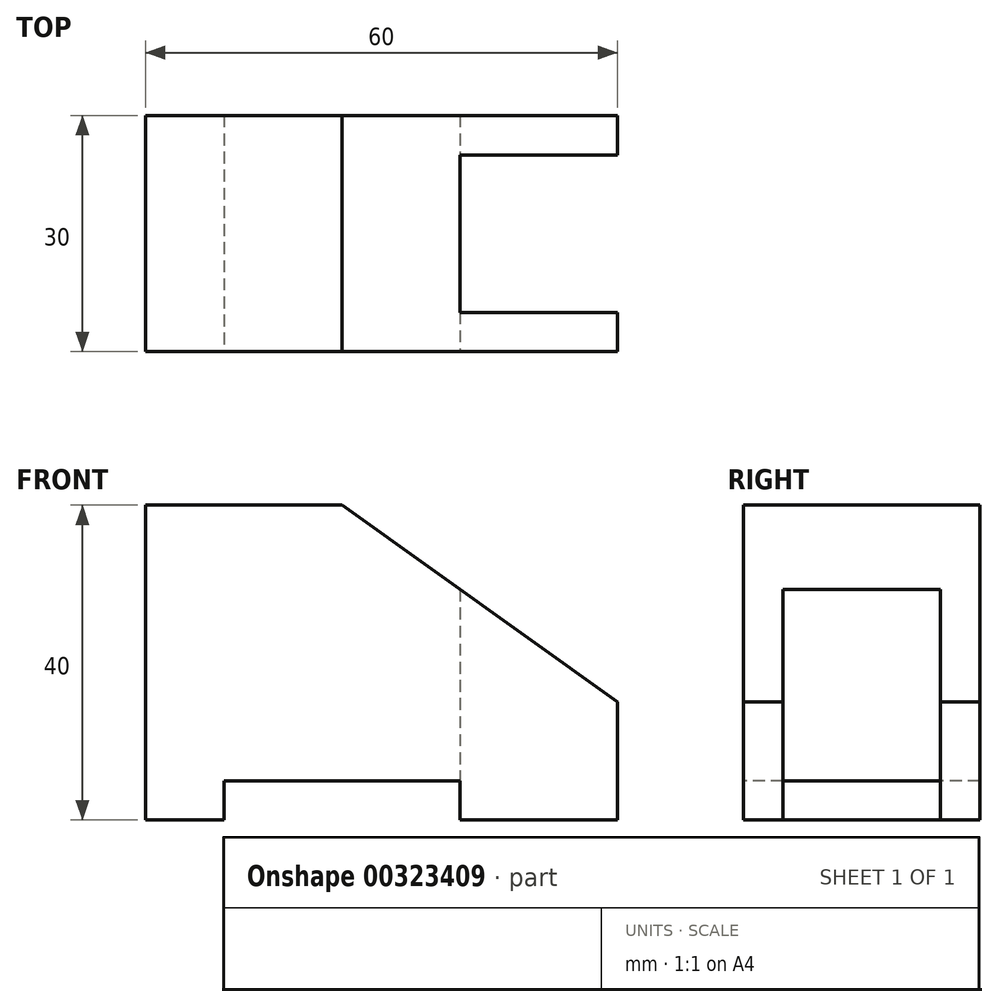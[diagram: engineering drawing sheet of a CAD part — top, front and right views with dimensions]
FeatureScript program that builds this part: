
annotation { "Feature Type Name" : "Feature", "Feature Type Description" : "" }
export const myFeature = defineFeature(function(context is Context, id is Id, definition is map)
    precondition{}
    {
        {
            var Q0;
            Q0=qCreatedBy(makeId("Front.planeOp"),FACE);
            var sketch = newSketch(context, id + "F0", { "sketchPlane" : qUnion([Q0])});
            skLineSegment(sketch, "E0.bottom", {"start": v(0, 0) * mm, "end": v(60, 0) * mm});
            skLineSegment(sketch, "E0.top", {"start": v(0, 40) * mm, "end": v(60, 40) * mm});
            skLineSegment(sketch, "E0.left", {"start": v(0, 0) * mm, "end": v(0, 40) * mm});
            skLineSegment(sketch, "E0.right", {"start": v(60, 0) * mm, "end": v(60, 40) * mm});
            skSolve(sketch);
        }
        {
            var Q0;
            Q0 = qSketchRegion(id + "F0", true);
            extrude(context, id + "F1", {"entities" : qUnion([Q0]), "oppositeDirection" : true, "depth" : 30 * mm});
        }
        {
            var Q0;
            Q0=makeQuery(id+"F1.opExtrude","CAP_FACE",FACE,{"disambiguationData":[OSD([sQuery(id+"F0.wireOp",EDGE,"E0.bottom"),sQuery(id+"F0.wireOp",EDGE,"E0.top"),sQuery(id+"F0.wireOp",EDGE,"E0.left"),sQuery(id+"F0.wireOp",EDGE,"E0.right")])],"isStart":true});
            var sketch = newSketch(context, id + "F2", { "sketchPlane" : qUnion([Q0])});
            skLineSegment(sketch, "E1", {"start": v(0, 0) * mm, "end": v(10, 0) * mm});
            skLineSegment(sketch, "E2.bottom", {"start": v(10, 0) * mm, "end": v(40, 0) * mm});
            skLineSegment(sketch, "E2.top", {"start": v(10, 5) * mm, "end": v(40, 5) * mm});
            skLineSegment(sketch, "E2.left", {"start": v(10, 0) * mm, "end": v(10, 5) * mm});
            skLineSegment(sketch, "E2.right", {"start": v(40, 0) * mm, "end": v(40, 5) * mm});
            skLineSegment(sketch, "E3", {"start": v(25, 40) * mm, "end": v(60, 40) * mm});
            skLineSegment(sketch, "E4", {"start": v(60, 40) * mm, "end": v(60, 15) * mm});
            skLineSegment(sketch, "E5", {"start": v(60, 15) * mm, "end": v(25, 40) * mm});
            skSolve(sketch);
        }
        {
            var Q0;
            Q0 = qSketchRegion(id + "F2", true);
            extrude(context, id + "F3", {"entities" : qUnion([Q0]), "operationType" : NewBodyOperationType.REMOVE, "endBound" : BoundingType.THROUGH_ALL, "oppositeDirection" : true, "depth" : 25 * mm});
        }
        {
            var Q0;
            Q0=makeQuery(id+"F1.opExtrude","SWEPT_FACE",FACE,{"disambiguationData":[OSD([sQuery(id+"F0.wireOp",EDGE,"E0.right")])]});
            cPlane(context, id + "F4", {"entities" : qUnion([Q0]), "cplaneType" : CPlaneType.OFFSET, "offset" : 0 * mm, "width" : 150 * mm, "height" : 150 * mm});
        }
        {
            var Q0;
            Q0=qCreatedBy(id+"F4.planeOp",FACE);
            var sketch = newSketch(context, id + "F5", { "sketchPlane" : qUnion([Q0])});
            skPoint(sketch, "E6.0", {"position": v(15, 0) * mm});
            skLineSegment(sketch, "E7.bottom", {"start": v(5, 30) * mm, "end": v(25, 30) * mm});
            skLineSegment(sketch, "E7.top", {"start": v(5, 0) * mm, "end": v(25, 0) * mm});
            skLineSegment(sketch, "E7.left", {"start": v(5, 30) * mm, "end": v(5, 0) * mm});
            skLineSegment(sketch, "E7.right", {"start": v(25, 30) * mm, "end": v(25, 0) * mm});
            skSolve(sketch);
        }
        {
            var Q0;
            Q0 = qSketchRegion(id + "F5", true);
            extrude(context, id + "F6", {"entities" : qUnion([Q0]), "operationType" : NewBodyOperationType.REMOVE, "oppositeDirection" : true, "depth" : 20 * mm});
        }
    });
